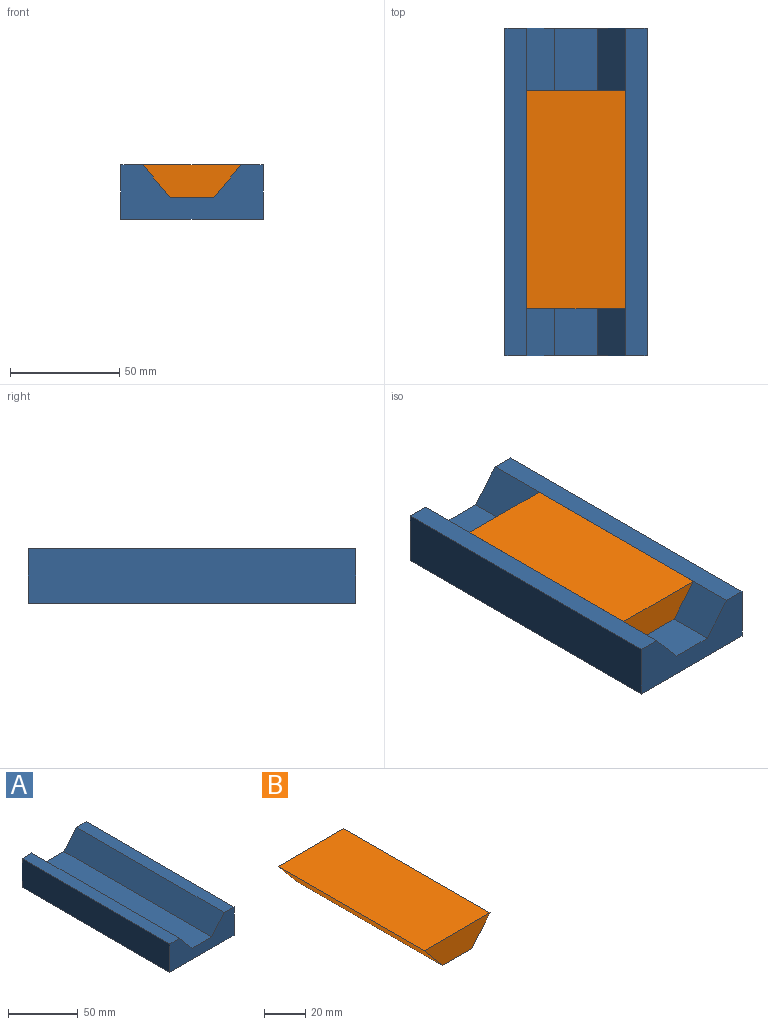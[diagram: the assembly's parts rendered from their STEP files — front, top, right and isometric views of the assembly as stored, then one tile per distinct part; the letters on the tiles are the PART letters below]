
ASSEMBLY  parts=2 mates=1
PART A: 10 faces, bbox 65.2x150x25 mm
  f0: plane 150x20mm, normal (0,0,1), area 3000mm2, adj f1,f7,f8,f9
  f1: plane 150x15mm, normal (0.77,0,0.64), area 2937.2mm2, adj f0,f2,f8,f9
  f2: plane 150x10mm, normal (0,0,1), area 1500mm2, adj f1,f3,f8,f9
  f3: plane 150x25mm, normal (-1,0,0), area 3750mm2, adj f2,f4,f8,f9
  f4: plane 150x65.17mm, normal (0,0,-1), area 9775.9mm2, adj f3,f5,f8,f9
  f5: plane 150x25mm, normal (1,0,0), area 3750mm2, adj f4,f6,f8,f9
  f6: plane 150x10mm, normal (0,0,1), area 1500mm2, adj f5,f7,f8,f9
  f7: plane 150x15mm, normal (-0.77,0,0.64), area 2937.2mm2, adj f0,f6,f8,f9
  f8: plane 65.17x25mm, normal (0,-1,0), area 1140.5mm2, adj f0,f1,f2,f3,f4,f5,f6,f7
  f9: plane 65.17x25mm, normal (0,1,0), area 1140.5mm2, adj f0,f1,f2,f3,f4,f5,f6,f7
PART B: 6 faces, bbox 45.2x100x15 mm
  f0: plane 100x15mm, normal (-0.77,0,-0.64), area 1958.1mm2, adj f1,f3,f4,f5
  f1: plane 100x20mm, normal (0,0,-1), area 2000mm2, adj f0,f2,f4,f5
  f2: plane 100x15mm, normal (0.77,0,-0.64), area 1958.1mm2, adj f1,f3,f4,f5
  f3: plane 100x45.17mm, normal (0,0,1), area 4517.3mm2, adj f0,f2,f4,f5
  f4: plane 45.17x15mm, normal (0,-1,0), area 488.8mm2, adj f0,f1,f2,f3
  f5: plane 45.17x15mm, normal (0,1,0), area 488.8mm2, adj f0,f1,f2,f3
PLACE A t=(8.3,36.32,9.9)mm
PLACE B t=(8.3,7.77,9.9)mm
MATE slider B.f4 <-> A.f8  axis (0,-1,0) through (8.3,-92.23,9.9)mm
